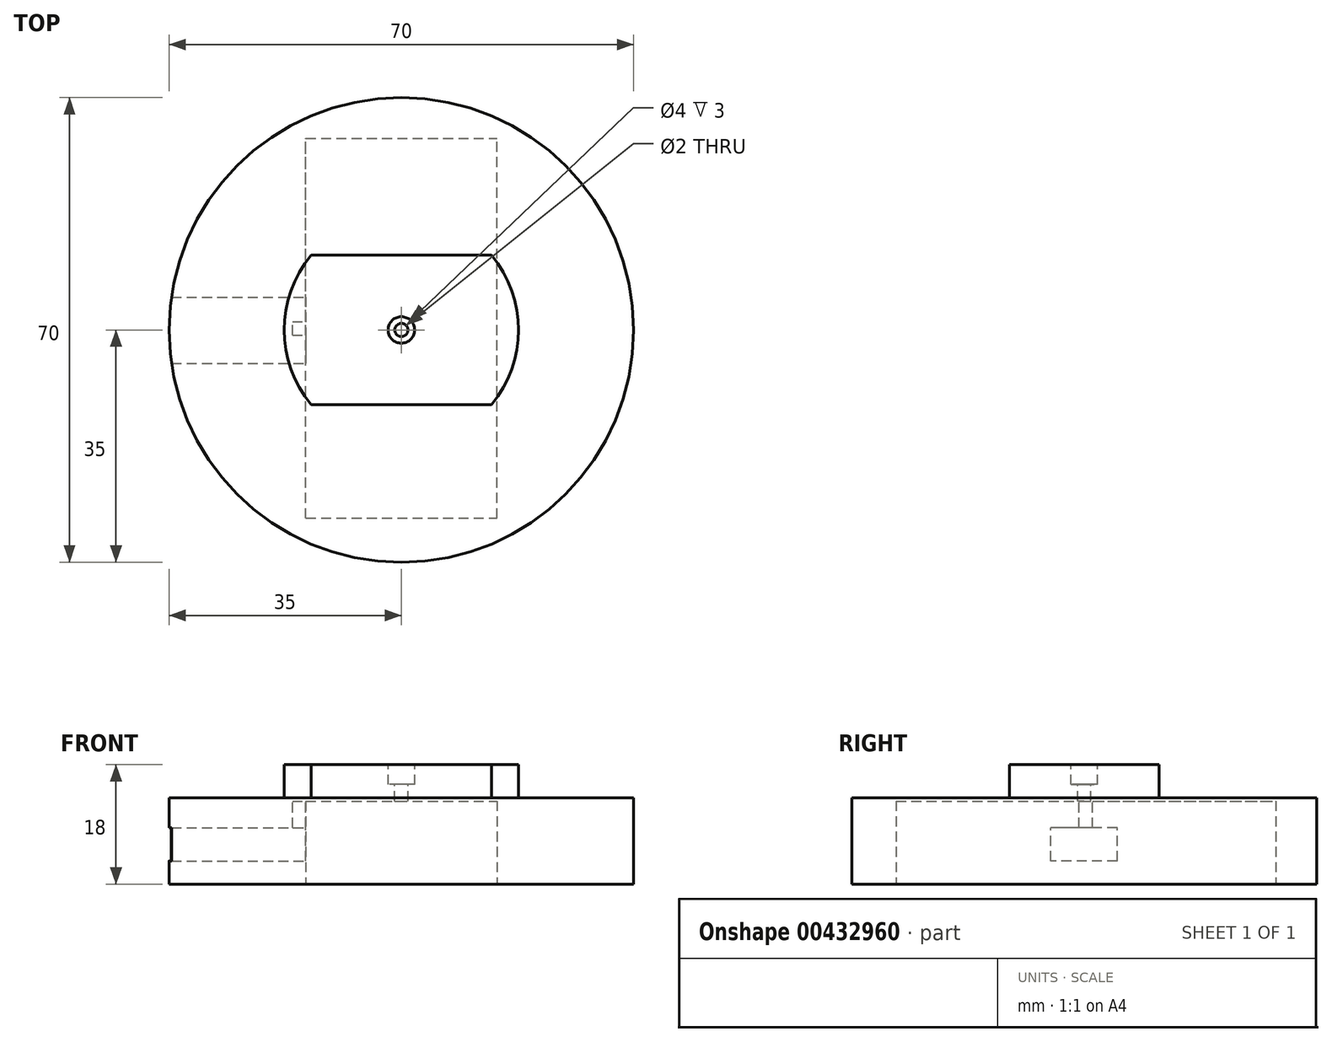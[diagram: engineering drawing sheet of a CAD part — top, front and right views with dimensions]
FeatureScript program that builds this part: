
annotation { "Feature Type Name" : "Feature", "Feature Type Description" : "" }
export const myFeature = defineFeature(function(context is Context, id is Id, definition is map)
    precondition{}
    {
        {
            var Q0;
            Q0=qCreatedBy(makeId("Top.planeOp"),FACE);
            var sketch = newSketch(context, id + "F0", { "sketchPlane" : qUnion([Q0])});
            skCircle(sketch, "E0", {"center": v(0, 0) * mm, "radius": 35 * mm});
            skSolve(sketch);
        }
        {
            var Q0;
            Q0=makeQuery(id+"F0.imprint","IMPRINT",FACE,{"disambiguationData":[TD([[makeQuery(id+"F0.imprint","IMPRINT",EDGE,{"derivedFrom":sQuery(id+"F0.wireOp",EDGE,"E0")}),1.0]])]});
            extrude(context, id + "F1", {"entities" : qUnion([Q0]), "depth" : 13 * mm});
        }
        {
            var Q0;
            Q0=makeQuery(id+"F1.opExtrude","CAP_FACE",FACE,{"disambiguationData":[OSD([sQuery(id+"F0.wireOp",EDGE,"E0")])],"isStart":true});
            var sketch = newSketch(context, id + "F2", { "sketchPlane" : qUnion([Q0])});
            skLineSegment(sketch, "E1.bottom", {"start": v(-14.4, 28.35) * mm, "end": v(14.4, 28.35) * mm});
            skLineSegment(sketch, "E1.top", {"start": v(-14.4, -28.85) * mm, "end": v(14.4, -28.85) * mm});
            skLineSegment(sketch, "E1.left", {"start": v(-14.4, 28.35) * mm, "end": v(-14.4, -28.85) * mm});
            skLineSegment(sketch, "E1.right", {"start": v(14.4, 28.35) * mm, "end": v(14.4, -28.85) * mm});
            skLineSegment(sketch, "E2", {"start": v(0, 0) * mm, "end": v(-14.4, 0) * mm});
            skLineSegment(sketch, "E3", {"start": v(0, 0) * mm, "end": v(14.4, 0) * mm});
            skSolve(sketch);
        }
        {
            var Q0;
            {var subQ2=sQuery(id+"F2.wireOp",EDGE,"E1.bottom");Q0=makeQuery(id+"F2.imprint","IMPRINT",FACE,{"disambiguationData":[TD([[makeQuery(id+"F2.imprint","IMPRINT",EDGE,{"derivedFrom":subQ2}),-1.0]])]});}
            var Q1;
            {var subQ1=sQuery(id+"F2.wireOp",EDGE,"E1.top");Q1=makeQuery(id+"F2.imprint","IMPRINT",FACE,{"disambiguationData":[TD([[makeQuery(id+"F2.imprint","IMPRINT",EDGE,{"derivedFrom":subQ1}),1.0]])]});}
            extrude(context, id + "F3", {"entities" : qUnion([Q0, Q1]), "operationType" : NewBodyOperationType.REMOVE, "oppositeDirection" : true, "depth" : 12.5 * mm});
        }
        {
            var Q0;
            Q0=makeQuery(id+"F1.opExtrude","CAP_FACE",FACE,{"disambiguationData":[OSD([sQuery(id+"F0.wireOp",EDGE,"E0")])],"isStart":false});
            var sketch = newSketch(context, id + "F4", { "sketchPlane" : qUnion([Q0])});
            skCircle(sketch, "E4", {"center": v(0, 0) * mm, "radius": 17.65 * mm});
            skLineSegment(sketch, "E5.bottom", {"start": v(0, 0) * mm, "end": v(0, 0) * mm});
            skLineSegment(sketch, "E5.top", {"start": v(0, -11.25) * mm, "end": v(0, -11.25) * mm});
            skLineSegment(sketch, "E6", {"start": v(0, -11.25) * mm, "end": v(13.6, -11.25) * mm});
            skLineSegment(sketch, "E7", {"start": v(0, -11.25) * mm, "end": v(-13.6, -11.25) * mm});
            skLineSegment(sketch, "E8", {"start": v(-13.6, 11.25) * mm, "end": v(13.6, 11.25) * mm});
            skSolve(sketch);
        }
        {
            var Q0;
            {var subQ1=sQuery(id+"F4.wireOp",EDGE,"E6");Q0=makeQuery(id+"F4.imprint","IMPRINT",FACE,{"disambiguationData":[TD([[makeQuery(id+"F4.imprint","IMPRINT",EDGE,{"derivedFrom":subQ1}),1.0]])]});}
            extrude(context, id + "F5", {"entities" : qUnion([Q0]), "operationType" : NewBodyOperationType.ADD, "depth" : 5 * mm});
        }
        {
            var Q0;
            Q0=makeQuery(id+"F5.opExtrude","CAP_FACE",FACE,{"disambiguationData":[OSD([sQuery(id+"F4.wireOp",EDGE,"E4"),sQuery(id+"F4.wireOp",EDGE,"E6"),sQuery(id+"F4.wireOp",EDGE,"E7"),sQuery(id+"F4.wireOp",EDGE,"E8")])],"isStart":false});
            var sketch = newSketch(context, id + "F6", { "sketchPlane" : qUnion([Q0])});
            skCircle(sketch, "E9", {"center": v(0, 0) * mm, "radius": 2 * mm});
            skSolve(sketch);
        }
        {
            var Q0;
            Q0=makeQuery(id+"F6.imprint","IMPRINT",FACE,{"disambiguationData":[TD([[makeQuery(id+"F6.imprint","IMPRINT",EDGE,{"derivedFrom":sQuery(id+"F6.wireOp",EDGE,"E9")}),1.0]])]});
            extrude(context, id + "F7", {"entities" : qUnion([Q0]), "operationType" : NewBodyOperationType.REMOVE, "oppositeDirection" : true, "depth" : 3 * mm});
        }
        {
            var Q0;
            Q0=makeQuery(id+"F7.boolean.opBoolean","COPY",FACE,{"derivedFrom":makeQuery(id+"F7.opExtrude","CAP_FACE",FACE,{"disambiguationData":[OSD([sQuery(id+"F6.wireOp",EDGE,"E9")])],"isStart":false})});
            var sketch = newSketch(context, id + "F8", { "sketchPlane" : qUnion([Q0])});
            skCircle(sketch, "E10", {"center": v(0, 0) * mm, "radius": 1 * mm});
            skSolve(sketch);
        }
        {
            var Q0;
            Q0=makeQuery(id+"F8.imprint","IMPRINT",FACE,{"disambiguationData":[TD([[makeQuery(id+"F8.imprint","IMPRINT",EDGE,{"derivedFrom":sQuery(id+"F8.wireOp",EDGE,"E10")}),1.0]])]});
            extrude(context, id + "F9", {"entities" : qUnion([Q0]), "operationType" : NewBodyOperationType.REMOVE, "oppositeDirection" : true, "depth" : 25 * mm});
        }
        {
            var Q0;
            Q0=makeQuery(id+"F3.boolean.opBoolean","COPY",FACE,{"derivedFrom":makeQuery(id+"F3.opExtrude","SWEPT_FACE",FACE,{"disambiguationData":[OSD([sQuery(id+"F2.wireOp",EDGE,"E1.left")])]})});
            var sketch = newSketch(context, id + "F10", { "sketchPlane" : qUnion([Q0])});
            skLineSegment(sketch, "E11.bottom", {"start": v(4.96, 3.48) * mm, "end": v(-5.04, 3.48) * mm});
            skLineSegment(sketch, "E11.top", {"start": v(4.96, 8.48) * mm, "end": v(-5.04, 8.48) * mm});
            skLineSegment(sketch, "E11.left", {"start": v(4.96, 3.48) * mm, "end": v(4.96, 8.48) * mm});
            skLineSegment(sketch, "E11.right", {"start": v(-5.04, 3.48) * mm, "end": v(-5.04, 8.48) * mm});
            skSolve(sketch);
        }
        {
            var Q0;
            Q0=makeQuery(id+"F10.imprint","IMPRINT",FACE,{"disambiguationData":[TD([[makeQuery(id+"F10.imprint","IMPRINT",EDGE,{"derivedFrom":sQuery(id+"F10.wireOp",EDGE,"E11.bottom")}),-1.0]])]});
            extrude(context, id + "F11", {"entities" : qUnion([Q0]), "operationType" : NewBodyOperationType.REMOVE, "oppositeDirection" : true, "depth" : 25 * mm});
        }
        {
            var Q0;
            Q0=makeQuery(id+"F3.boolean.opBoolean","COPY",FACE,{"derivedFrom":makeQuery(id+"F3.opExtrude","SWEPT_FACE",FACE,{"disambiguationData":[OSD([sQuery(id+"F2.wireOp",EDGE,"E1.left")])]})});
            var sketch = newSketch(context, id + "F12", { "sketchPlane" : qUnion([Q0])});
            skLineSegment(sketch, "E12.bottom", {"start": v(1.22, 8.48) * mm, "end": v(-0.76, 8.48) * mm});
            skLineSegment(sketch, "E12.top", {"start": v(1.22, 12.5) * mm, "end": v(-0.76, 12.5) * mm});
            skLineSegment(sketch, "E12.left", {"start": v(1.22, 8.48) * mm, "end": v(1.22, 12.5) * mm});
            skLineSegment(sketch, "E12.right", {"start": v(-0.76, 8.48) * mm, "end": v(-0.76, 12.5) * mm});
            skSolve(sketch);
        }
        {
            var Q0;
            Q0=makeQuery(id+"F12.imprint","IMPRINT",FACE,{"disambiguationData":[TD([[makeQuery(id+"F12.imprint","IMPRINT",EDGE,{"derivedFrom":sQuery(id+"F12.wireOp",EDGE,"E12.bottom")}),-1.0]])]});
            extrude(context, id + "F13", {"entities" : qUnion([Q0]), "operationType" : NewBodyOperationType.REMOVE, "oppositeDirection" : true, "depth" : 2 * mm});
        }
    });
